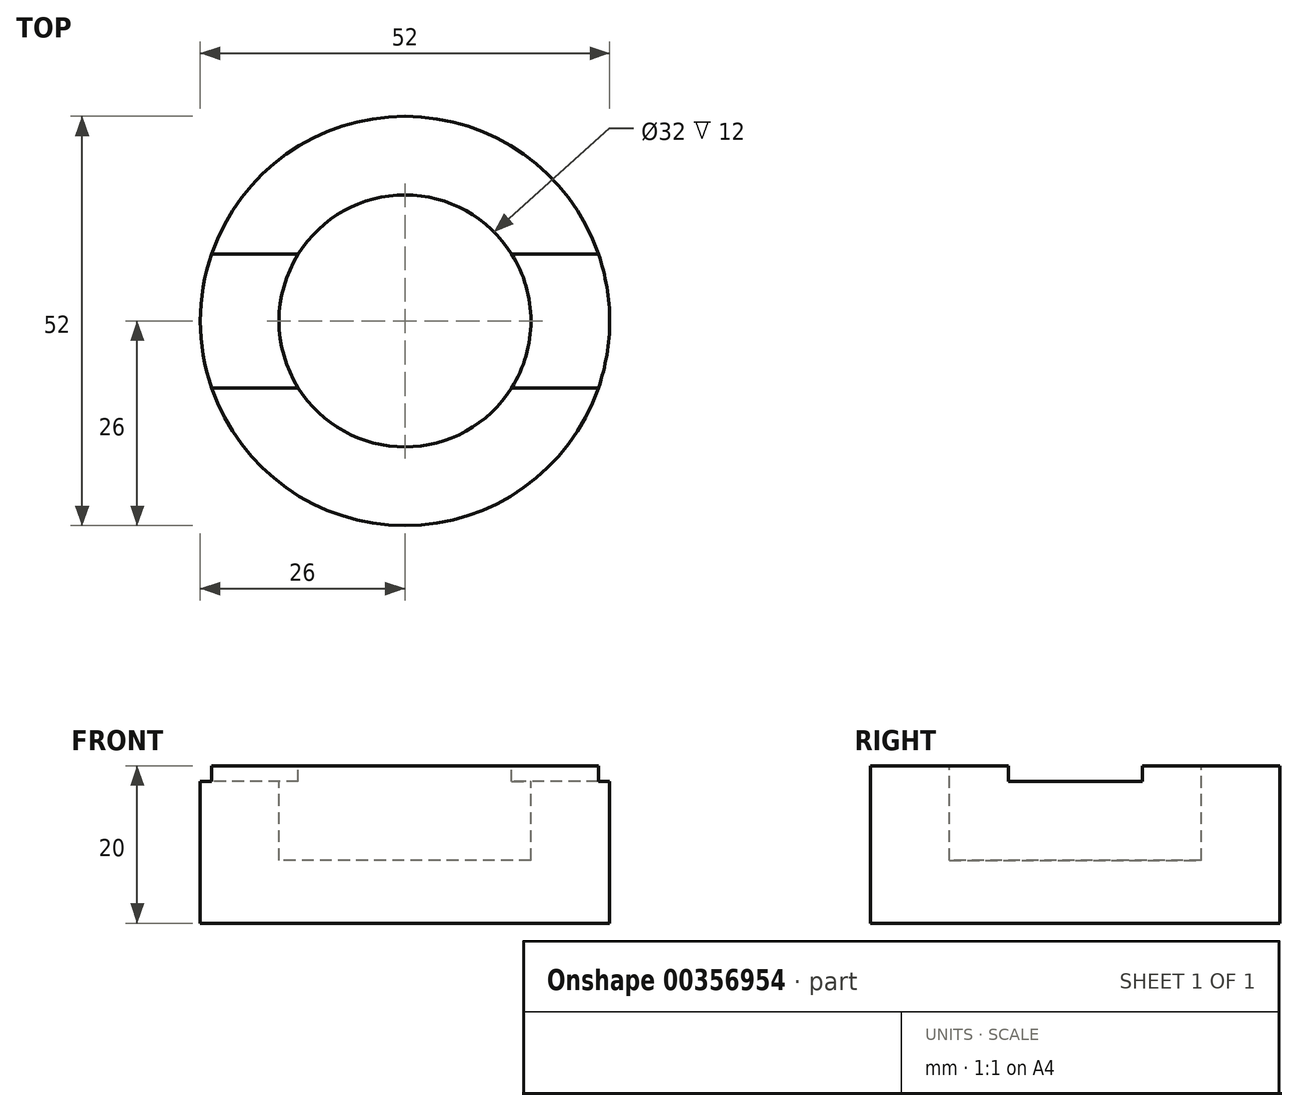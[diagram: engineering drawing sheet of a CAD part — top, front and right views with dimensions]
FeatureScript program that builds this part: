
annotation { "Feature Type Name" : "Feature", "Feature Type Description" : "" }
export const myFeature = defineFeature(function(context is Context, id is Id, definition is map)
    precondition{}
    {
        {
            var Q0;
            Q0=qCreatedBy(makeId("Top.planeOp"),FACE);
            var sketch = newSketch(context, id + "F0", { "sketchPlane" : qUnion([Q0])});
            skCircle(sketch, "E0", {"center": v(0, 0) * mm, "radius": 16 * mm});
            skCircle(sketch, "E1", {"center": v(0, 0) * mm, "radius": 26 * mm});
            skSolve(sketch);
        }
        {
            var Q0;
            Q0=makeQuery(id+"F0.imprint","IMPRINT",FACE,{"disambiguationData":[TD([[makeQuery(id+"F0.imprint","IMPRINT",EDGE,{"derivedFrom":sQuery(id+"F0.wireOp",EDGE,"E0")}),-1.0]])]});
            var Q1;
            Q1=makeQuery(id+"F0.imprint","IMPRINT",FACE,{"disambiguationData":[TD([[makeQuery(id+"F0.imprint","IMPRINT",EDGE,{"derivedFrom":sQuery(id+"F0.wireOp",EDGE,"E0")}),1.0]])]});
            extrude(context, id + "F1", {"entities" : qUnion([Q0, Q1]), "oppositeDirection" : true, "depth" : 20 * mm});
        }
        {
            var Q0;
            Q0=makeQuery(id+"F0.imprint","IMPRINT",FACE,{"disambiguationData":[TD([[makeQuery(id+"F0.imprint","IMPRINT",EDGE,{"derivedFrom":sQuery(id+"F0.wireOp",EDGE,"E0")}),1.0]])]});
            extrude(context, id + "F2", {"entities" : qUnion([Q0]), "operationType" : NewBodyOperationType.REMOVE, "oppositeDirection" : true, "depth" : 12 * mm});
        }
        {
            var Q0;
            Q0=qCreatedBy(makeId("Top.planeOp"),FACE);
            var sketch = newSketch(context, id + "F3", { "sketchPlane" : qUnion([Q0])});
            skLineSegment(sketch, "E2.bottom", {"start": v(26, -8.5) * mm, "end": v(-26, -8.5) * mm});
            skLineSegment(sketch, "E2.top", {"start": v(26, 8.5) * mm, "end": v(-26, 8.5) * mm});
            skLineSegment(sketch, "E2.left", {"start": v(26, -8.5) * mm, "end": v(26, 8.5) * mm});
            skLineSegment(sketch, "E2.right", {"start": v(-26, -8.5) * mm, "end": v(-26, 8.5) * mm});
            skPoint(sketch, "E2.middle", {"position": v(0, 0) * mm});
            skSolve(sketch);
        }
        {
            var Q0;
            Q0 = qSketchRegion(id + "F3", true);
            extrude(context, id + "F4", {"entities" : qUnion([Q0]), "operationType" : NewBodyOperationType.REMOVE, "oppositeDirection" : true, "depth" : 2 * mm});
        }
    });
